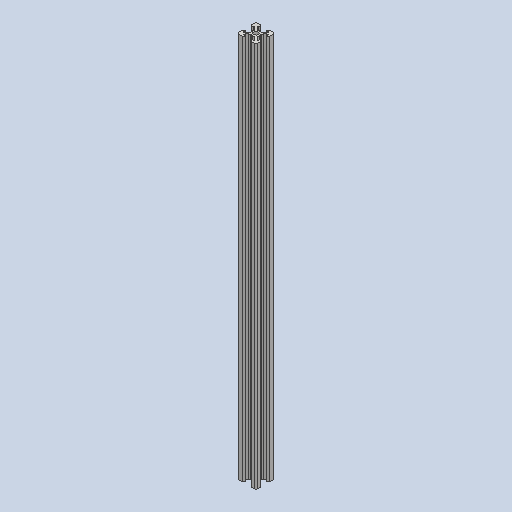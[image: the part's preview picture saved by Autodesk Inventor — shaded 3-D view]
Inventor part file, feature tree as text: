
AUTODESK INVENTOR PART (.ipt)
format: ipt  version: 2025.2 (Build 292293000, 293)  size: 408,064 bytes
history: native  units: mm
features: other x1, extrude x1, sketch x1
ambient origin geometry x8: Origin, YZ Plane, XZ Plane, XY Plane, X Axis, Y Axis, Z Axis, Center Point
bodies: Body1 (feature_tree)
feature tree (3):
  other  "Твердое тело1"
  extrude  "Выдавливание1"  Depth=0.25mm
  sketch  "Эскиз1"
